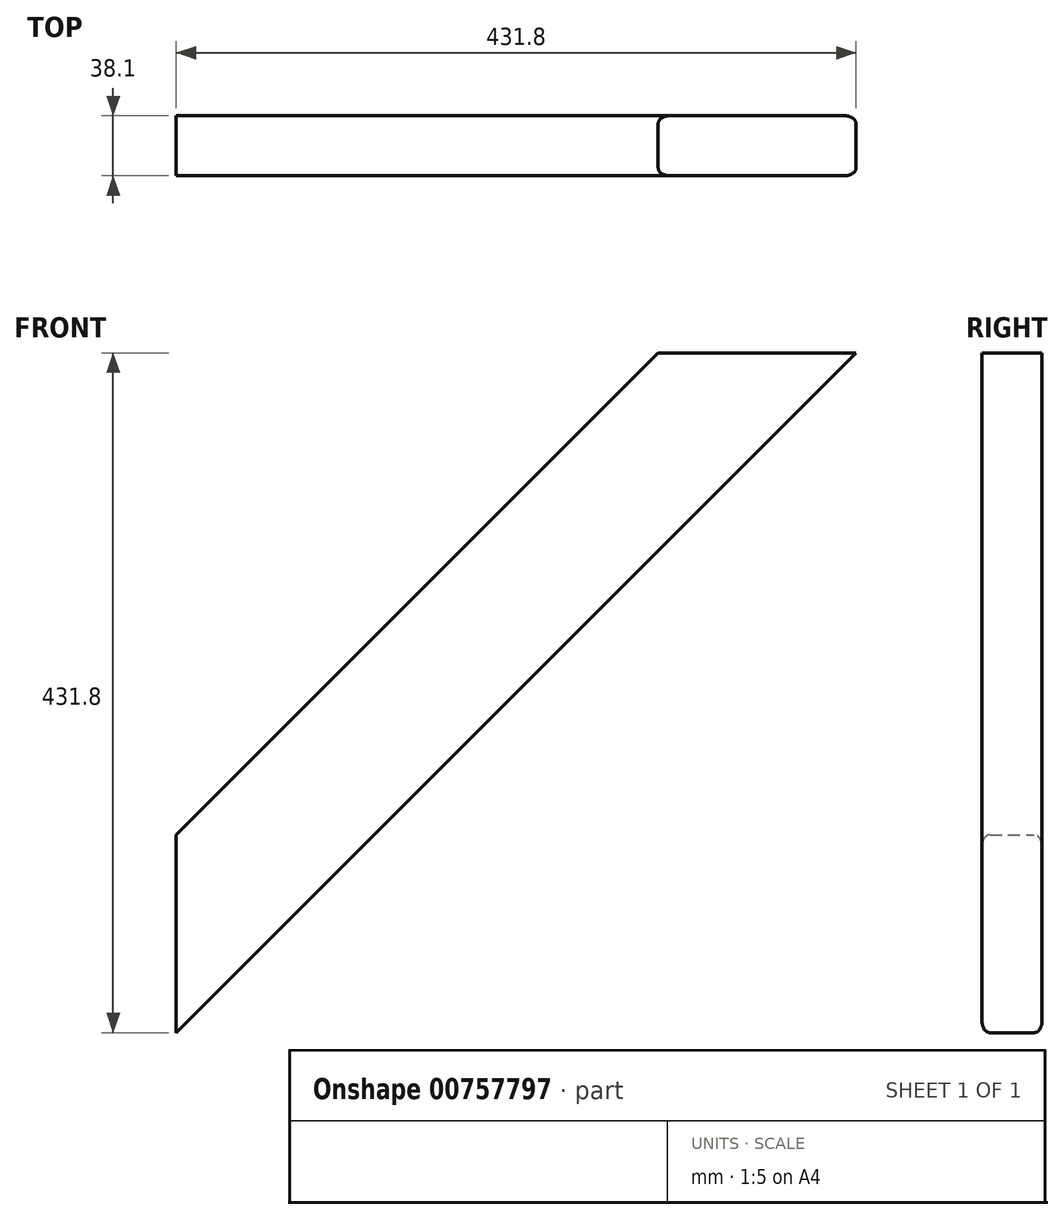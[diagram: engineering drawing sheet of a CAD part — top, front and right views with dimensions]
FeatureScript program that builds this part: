
annotation { "Feature Type Name" : "Feature", "Feature Type Description" : "" }
export const myFeature = defineFeature(function(context is Context, id is Id, definition is map)
    precondition{}
    {
        {
            var Q0;
            Q0=qCreatedBy(makeId("Front.planeOp"),FACE);
            var sketch = newSketch(context, id + "F0", { "sketchPlane" : qUnion([Q0])});
            skLineSegment(sketch, "E0", {"start": v(-187.04, -174.6) * mm, "end": v(244.76, 257.2) * mm});
            skLineSegment(sketch, "E1", {"start": v(244.76, 257.2) * mm, "end": v(-187.04, 257.2) * mm});
            skLineSegment(sketch, "E2", {"start": v(-187.04, 257.2) * mm, "end": v(-187.04, -174.6) * mm});
            skLineSegment(sketch, "E3", {"start": v(-98.14, 168.3) * mm, "end": v(30.14, 168.3) * mm});
            skLineSegment(sketch, "E4", {"start": v(30.14, 168.3) * mm, "end": v(-98.14, 40.02) * mm});
            skLineSegment(sketch, "E5", {"start": v(-98.14, 40.02) * mm, "end": v(-98.14, 168.3) * mm});
            skLineSegment(sketch, "E6", {"start": v(-98.14, 40.02) * mm, "end": v(-187.04, -48.88) * mm});
            skLineSegment(sketch, "E7", {"start": v(30.14, 168.3) * mm, "end": v(119.04, 257.2) * mm});
            skSolve(sketch);
        }
        {
            var Q0;
            {var subQ1=sQuery(id+"F0.wireOp",EDGE,"E0");Q0=makeQuery(id+"F0.imprint","IMPRINT",FACE,{"disambiguationData":[TD([[makeQuery(id+"F0.imprint","IMPRINT",EDGE,{"derivedFrom":subQ1}),1.0]])]});}
            extrude(context, id + "F1", {"entities" : qUnion([Q0]), "depth" : 38.1 * mm, "offsetDistance" : 25.4 * mm});
        }
        {
            var Q0;
            Q0=makeQuery(id+"F1.opExtrude","CAP_EDGE",EDGE,{"disambiguationData":[OSD([sQuery(id+"F0.wireOp",EDGE,"E4"),sQuery(id+"F0.wireOp",EDGE,"E6"),sQuery(id+"F0.wireOp",EDGE,"E7")])],"isStart":true});
            var Q1;
            Q1=makeQuery(id+"F1.opExtrude","CAP_EDGE",EDGE,{"disambiguationData":[OSD([sQuery(id+"F0.wireOp",EDGE,"E4"),sQuery(id+"F0.wireOp",EDGE,"E6"),sQuery(id+"F0.wireOp",EDGE,"E7")])],"isStart":false});
            var Q2;
            Q2=makeQuery(id+"F1.opExtrude","CAP_EDGE",EDGE,{"disambiguationData":[OSD([sQuery(id+"F0.wireOp",EDGE,"E0")])],"isStart":false});
            var Q3;
            Q3=makeQuery(id+"F1.opExtrude","CAP_EDGE",EDGE,{"disambiguationData":[OSD([sQuery(id+"F0.wireOp",EDGE,"E0")])],"isStart":true});
            fillet(context, id + "F2", {"entities" : qUnion([Q0, Q1, Q2, Q3]), "radius" : 5.08 * mm, "tangentPropagation" : true, "allowEdgeOverflow" : false});
        }
    });
